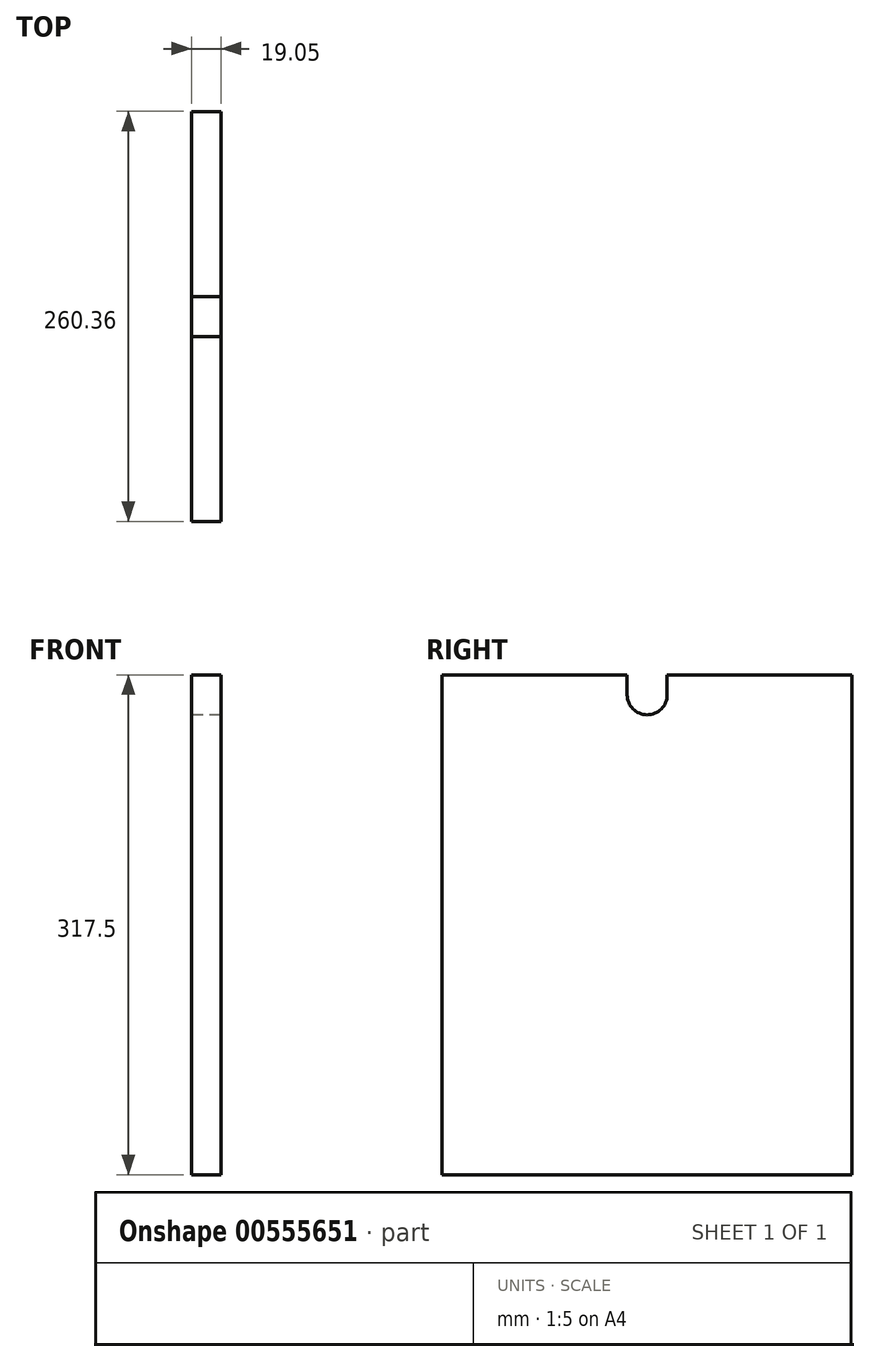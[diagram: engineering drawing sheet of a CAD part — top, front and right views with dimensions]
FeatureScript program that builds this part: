
annotation { "Feature Type Name" : "Feature", "Feature Type Description" : "" }
export const myFeature = defineFeature(function(context is Context, id is Id, definition is map)
    precondition{}
    {
        {
            var Q0;
            Q0=qCreatedBy(makeId("Right.planeOp"),FACE);
            var sketch = newSketch(context, id + "F0", { "sketchPlane" : qUnion([Q0])});
            skLineSegment(sketch, "E0.bottom", {"start": v(130.17, 158.75) * mm, "end": v(-130.18, 158.75) * mm});
            skLineSegment(sketch, "E0.top", {"start": v(130.18, -158.75) * mm, "end": v(-130.17, -158.75) * mm});
            skLineSegment(sketch, "E0.left", {"start": v(130.17, 158.75) * mm, "end": v(130.18, -158.75) * mm});
            skLineSegment(sketch, "E0.right", {"start": v(-130.18, 158.75) * mm, "end": v(-130.17, -158.75) * mm});
            skPoint(sketch, "E0.middle", {"position": v(0, 0) * mm});
            skCircle(sketch, "E1", {"center": v(0, 146.05) * mm, "radius": 12.7 * mm});
            skLineSegment(sketch, "E2", {"start": v(-12.7, 146.05) * mm, "end": v(-12.7, 158.75) * mm});
            skLineSegment(sketch, "E3", {"start": v(12.7, 146.05) * mm, "end": v(12.7, 158.75) * mm});
            skSolve(sketch);
        }
        {
            var Q0;
            Q0=makeQuery(id+"F0.imprint","IMPRINT",FACE,{"disambiguationData":[TD([[makeQuery(id+"F0.imprint","IMPRINT",EDGE,{"derivedFrom":sQuery(id+"F0.wireOp",EDGE,"E0.top")}),-1.0]])]});
            extrude(context, id + "F1", {"entities" : qUnion([Q0]), "depth" : 19.05 * mm, "offsetDistance" : 25.4 * mm});
        }
    });
